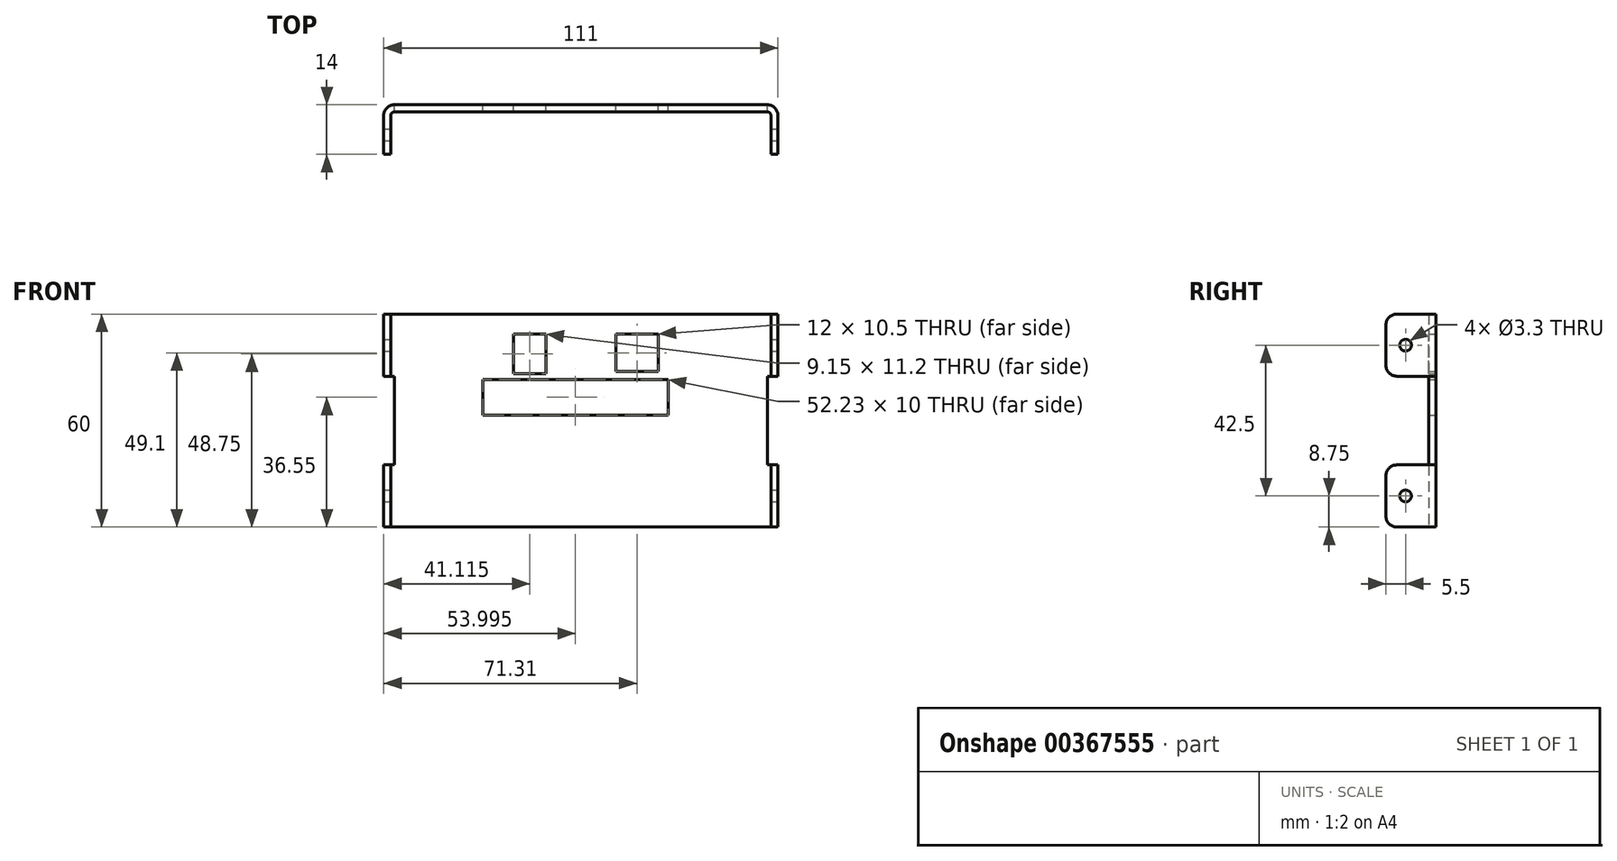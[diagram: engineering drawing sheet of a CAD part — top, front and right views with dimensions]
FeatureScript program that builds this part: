
annotation { "Feature Type Name" : "Feature", "Feature Type Description" : "" }
export const myFeature = defineFeature(function(context is Context, id is Id, definition is map)
    precondition{}
    {
        {
            var Q0;
            Q0=qCreatedBy(makeId("Top.planeOp"),FACE);
            var sketch = newSketch(context, id + "F0", { "sketchPlane" : qUnion([Q0])});
            skLineSegment(sketch, "E0", {"start": v(52.5, 0) * mm, "end": v(-52.5, 0) * mm});
            skLineSegment(sketch, "E1", {"start": v(-53.5, -1) * mm, "end": v(-53.5, -12) * mm});
            skLineSegment(sketch, "E2", {"start": v(53.5, -1) * mm, "end": v(53.5, -12) * mm});
            skPoint(sketch, "E3", {"position": v(0, 0) * mm});
            skPoint(sketch, "E4.visualSharp", {"position": v(-53.5, 0) * mm});
            skArc(sketch, "E4.filletArc", {"start": v(-52.5, 0) * mm, "mid": v(-53.2, -0.3) * mm, "end": v(-53.5, -1) * mm});
            skPoint(sketch, "E5.visualSharp", {"position": v(53.5, 0) * mm});
            skArc(sketch, "E5.filletArc", {"start": v(53.5, -1) * mm, "mid": v(53.2, -0.3) * mm, "end": v(52.5, 0) * mm});
            skLineSegment(sketch, "E6.0", {"start": v(-55.5, -1) * mm, "end": v(-55.5, -12) * mm});
            skLineSegment(sketch, "E6.1", {"start": v(55.5, -1) * mm, "end": v(55.5, -12) * mm});
            skArc(sketch, "E6.2", {"start": v(55.5, -1) * mm, "mid": v(54.62, 1.12) * mm, "end": v(52.5, 2) * mm});
            skLineSegment(sketch, "E6.3", {"start": v(52.5, 2) * mm, "end": v(-52.5, 2) * mm});
            skArc(sketch, "E6.4", {"start": v(-52.5, 2) * mm, "mid": v(-54.62, 1.12) * mm, "end": v(-55.5, -1) * mm});
            skLineSegment(sketch, "E7", {"start": v(-55.5, -12) * mm, "end": v(-53.5, -12) * mm});
            skLineSegment(sketch, "E8", {"start": v(53.5, -12) * mm, "end": v(55.5, -12) * mm});
            skSolve(sketch);
        }
        {
            var Q0;
            Q0=makeQuery(id+"F0.imprint","IMPRINT",FACE,{"disambiguationData":[TD([[makeQuery(id+"F0.imprint","IMPRINT",EDGE,{"derivedFrom":sQuery(id+"F0.wireOp",EDGE,"E0")}),-1.0]])]});
            extrude(context, id + "F1", {"entities" : qUnion([Q0]), "endBound" : BoundingType.SYMMETRIC, "depth" : 60 * mm});
        }
        {
            var Q0;
            Q0=makeQuery(id+"F1.opExtrude","SWEPT_FACE",FACE,{"disambiguationData":[OSD([sQuery(id+"F0.wireOp",EDGE,"E6.3")])]});
            var sketch = newSketch(context, id + "F2", { "sketchPlane" : qUnion([Q0])});
            skLineSegment(sketch, "E9.0", {"start": v(-55.5, 30) * mm, "end": v(-55.5, -30) * mm, "construction": true});
            skLineSegment(sketch, "E10.0", {"start": v(55.5, 30) * mm, "end": v(55.5, -30) * mm, "construction": true});
            skLineSegment(sketch, "E11.bottom", {"start": v(-55.5, 12.5) * mm, "end": v(-52.5, 12.5) * mm});
            skLineSegment(sketch, "E11.top", {"start": v(-55.5, -12.5) * mm, "end": v(-52.5, -12.5) * mm});
            skLineSegment(sketch, "E11.left", {"start": v(-55.5, 12.5) * mm, "end": v(-55.5, -12.5) * mm});
            skLineSegment(sketch, "E11.right", {"start": v(-52.5, 12.5) * mm, "end": v(-52.5, -12.5) * mm});
            skPoint(sketch, "E12", {"position": v(-52.5, 0) * mm});
            skLineSegment(sketch, "E13", {"start": v(0, 0) * mm, "end": v(0, 30) * mm, "construction": true});
            skLineSegment(sketch, "E14.MirrorCS", {"start": v(55.5, 12.5) * mm, "end": v(52.5, 12.5) * mm});
            skLineSegment(sketch, "E15.MirrorCS", {"start": v(55.5, -12.5) * mm, "end": v(52.5, -12.5) * mm});
            skPoint(sketch, "E16.MirrorP", {"position": v(52.5, 0) * mm});
            skLineSegment(sketch, "E17.MirrorCS", {"start": v(55.5, 12.5) * mm, "end": v(55.5, -12.5) * mm});
            skLineSegment(sketch, "E18.MirrorCS", {"start": v(52.5, 12.5) * mm, "end": v(52.5, -12.5) * mm});
            skLineSegment(sketch, "E19", {"start": v(-17.5, 26) * mm, "end": v(17.5, 26) * mm, "construction": true});
            skPoint(sketch, "E20", {"position": v(0, 26) * mm});
            skLineSegment(sketch, "E21.bottom", {"start": v(-21.81, 24.35) * mm, "end": v(-9.8, 24.35) * mm});
            skLineSegment(sketch, "E21.top", {"start": v(-21.81, 13.85) * mm, "end": v(-9.8, 13.85) * mm});
            skLineSegment(sketch, "E21.left", {"start": v(-21.81, 24.35) * mm, "end": v(-21.81, 13.85) * mm});
            skLineSegment(sketch, "E21.right", {"start": v(-9.8, 24.35) * mm, "end": v(-9.8, 13.85) * mm});
            skLineSegment(sketch, "E22.bottom", {"start": v(9.8, 24.35) * mm, "end": v(18.96, 24.35) * mm});
            skLineSegment(sketch, "E22.top", {"start": v(9.81, 13.15) * mm, "end": v(18.96, 13.15) * mm});
            skLineSegment(sketch, "E22.left", {"start": v(9.8, 24.35) * mm, "end": v(9.81, 13.15) * mm});
            skLineSegment(sketch, "E22.right", {"start": v(18.96, 24.35) * mm, "end": v(18.96, 13.15) * mm});
            skLineSegment(sketch, "E23", {"start": v(9.8, 24.35) * mm, "end": v(-9.8, 24.35) * mm, "construction": true});
            skPoint(sketch, "E24", {"position": v(0, 24.35) * mm});
            skLineSegment(sketch, "E25.bottom", {"start": v(-24.61, 11.55) * mm, "end": v(27.62, 11.55) * mm});
            skLineSegment(sketch, "E25.top", {"start": v(-24.61, 1.55) * mm, "end": v(27.62, 1.55) * mm});
            skLineSegment(sketch, "E25.left", {"start": v(-24.61, 11.55) * mm, "end": v(-24.61, 1.55) * mm});
            skLineSegment(sketch, "E25.right", {"start": v(27.62, 11.55) * mm, "end": v(27.62, 1.55) * mm});
            skSolve(sketch);
        }
        {
            var Q0;
            Q0=makeQuery(id+"F2.imprint","IMPRINT",FACE,{"disambiguationData":[TD([[makeQuery(id+"F2.imprint","IMPRINT",EDGE,{"derivedFrom":sQuery(id+"F2.wireOp",EDGE,"E11.bottom")}),-1.0]])]});
            var Q1;
            Q1=makeQuery(id+"F2.imprint","IMPRINT",FACE,{"disambiguationData":[TD([[makeQuery(id+"F2.imprint","IMPRINT",EDGE,{"derivedFrom":sQuery(id+"F2.wireOp",EDGE,"E14.MirrorCS")}),1.0]])]});
            var Q2;
            Q2=makeQuery(id+"F2.imprint","IMPRINT",FACE,{"disambiguationData":[TD([[makeQuery(id+"F2.imprint","IMPRINT",EDGE,{"derivedFrom":sQuery(id+"F2.wireOp",EDGE,"E21.bottom")}),-1.0]])]});
            var Q3;
            Q3=makeQuery(id+"F2.imprint","IMPRINT",FACE,{"disambiguationData":[TD([[makeQuery(id+"F2.imprint","IMPRINT",EDGE,{"derivedFrom":sQuery(id+"F2.wireOp",EDGE,"E22.bottom")}),-1.0]])]});
            var Q4;
            Q4=makeQuery(id+"F2.imprint","IMPRINT",FACE,{"disambiguationData":[TD([[makeQuery(id+"F2.imprint","IMPRINT",EDGE,{"derivedFrom":sQuery(id+"F2.wireOp",EDGE,"E25.bottom")}),-1.0]])]});
            extrude(context, id + "F3", {"entities" : qUnion([Q0, Q1, Q2, Q3, Q4]), "operationType" : NewBodyOperationType.REMOVE, "endBound" : BoundingType.THROUGH_ALL, "oppositeDirection" : true, "depth" : 25 * mm});
        }
        {
            var Q0;
            {var subQ2=sQuery(id+"F0.wireOp",EDGE,"E6.1");Q0=makeQuery(id+"F3.boolean.opBoolean","SPLIT",FACE,{"disambiguationData":[TD([makeQuery(id+"F3.opExtrude","SWEPT_FACE",FACE,{"disambiguationData":[OSD([sQuery(id+"F2.wireOp",EDGE,"E11.bottom")])]})])],"derivedFrom":makeQuery(id+"F1.opExtrude","SWEPT_FACE",FACE,{"disambiguationData":[OSD([subQ2])]})});}
            var sketch = newSketch(context, id + "F4", { "sketchPlane" : qUnion([Q0])});
            skLineSegment(sketch, "E26", {"start": v(-1, 12.5) * mm, "end": v(-12, 30) * mm, "construction": true});
            skLineSegment(sketch, "E27.0.0", {"start": v(-1, -12.5) * mm, "end": v(-12, -12.5) * mm, "construction": true});
            skLineSegment(sketch, "E27.0.1", {"start": v(-12, -12.5) * mm, "end": v(-12, -30) * mm, "construction": true});
            skLineSegment(sketch, "E27.0.2", {"start": v(-12, -30) * mm, "end": v(-1, -30) * mm, "construction": true});
            skLineSegment(sketch, "E27.0.3", {"start": v(-1, -30) * mm, "end": v(-1, -12.5) * mm, "construction": true});
            skLineSegment(sketch, "E28", {"start": v(-1, -30) * mm, "end": v(-12, -12.5) * mm, "construction": true});
            skPoint(sketch, "E29", {"position": v(-6.5, 21.25) * mm});
            skPoint(sketch, "E30", {"position": v(-6.5, -21.25) * mm});
            skSolve(sketch);
        }
        {
            var Q0;
            Q0=sQuery(id+"F4.wireOp",VERTEX,"E29");
            var Q1;
            Q1=sQuery(id+"F4.wireOp",VERTEX,"E30");
            var Q2;
            Q2=makeQuery(id+"F1.opExtrude","SWEPT_BODY",BODY,{"disambiguationData":[OSD([sQuery(id+"F0.wireOp",EDGE,"E0"),sQuery(id+"F0.wireOp",EDGE,"E1"),sQuery(id+"F0.wireOp",EDGE,"E2"),sQuery(id+"F0.wireOp",EDGE,"E4.filletArc"),sQuery(id+"F0.wireOp",EDGE,"E5.filletArc"),sQuery(id+"F0.wireOp",EDGE,"E6.0"),sQuery(id+"F0.wireOp",EDGE,"E6.1"),sQuery(id+"F0.wireOp",EDGE,"E6.2"),sQuery(id+"F0.wireOp",EDGE,"E6.3"),sQuery(id+"F0.wireOp",EDGE,"E6.4"),sQuery(id+"F0.wireOp",EDGE,"E7"),sQuery(id+"F0.wireOp",EDGE,"E8")])]});
            hole(context, id + "F5", {"style" : HoleStyle.SIMPLE, "endStyle" : HoleEndStyle.THROUGH, "standardTappedOrClearance" : lookupTablePath({ "standard" : "ISO", "fit" : "Normal", "size" : "M3", "type" : "Clearance" }), "standardBlindInLast" : lookupTablePath({ "fit" : "Standard", "standard" : "ISO", "size" : "M3", "type" : "Clearance" }), "holeDiameter" : 3.3 * mm, "tappedDepth" : 12 * mm, "tapClearance" : 3, "locations" : qUnion([Q0, Q1]), "scope" : qUnion([Q2])});
        }
        {
            var Q0;
            Q0=makeQuery(id+"F1.opExtrude","CAP_EDGE",EDGE,{"disambiguationData":[OSD([sQuery(id+"F0.wireOp",EDGE,"E7")])],"isStart":false});
            var Q1;
            Q1=makeQuery(id+"F3.boolean.opBoolean","INTERSECT",EDGE,{"derivedFrom":[makeQuery(id+"F1.opExtrude","SWEPT_FACE",FACE,{"disambiguationData":[OSD([sQuery(id+"F0.wireOp",EDGE,"E7")])]}),makeQuery(id+"F3.opExtrude","SWEPT_FACE",FACE,{"disambiguationData":[OSD([sQuery(id+"F2.wireOp",EDGE,"E14.MirrorCS")])]})]});
            var Q2;
            Q2=makeQuery(id+"F3.boolean.opBoolean","INTERSECT",EDGE,{"derivedFrom":[makeQuery(id+"F1.opExtrude","SWEPT_FACE",FACE,{"disambiguationData":[OSD([sQuery(id+"F0.wireOp",EDGE,"E7")])]}),makeQuery(id+"F3.opExtrude","SWEPT_FACE",FACE,{"disambiguationData":[OSD([sQuery(id+"F2.wireOp",EDGE,"E15.MirrorCS")])]})]});
            var Q3;
            Q3=makeQuery(id+"F1.opExtrude","CAP_EDGE",EDGE,{"disambiguationData":[OSD([sQuery(id+"F0.wireOp",EDGE,"E7")])],"isStart":true});
            var Q4;
            Q4=makeQuery(id+"F1.opExtrude","CAP_EDGE",EDGE,{"disambiguationData":[OSD([sQuery(id+"F0.wireOp",EDGE,"E8")])],"isStart":false});
            var Q5;
            Q5=makeQuery(id+"F3.boolean.opBoolean","INTERSECT",EDGE,{"derivedFrom":[makeQuery(id+"F1.opExtrude","SWEPT_FACE",FACE,{"disambiguationData":[OSD([sQuery(id+"F0.wireOp",EDGE,"E8")])]}),makeQuery(id+"F3.opExtrude","SWEPT_FACE",FACE,{"disambiguationData":[OSD([sQuery(id+"F2.wireOp",EDGE,"E11.bottom")])]})]});
            var Q6;
            Q6=makeQuery(id+"F3.boolean.opBoolean","INTERSECT",EDGE,{"derivedFrom":[makeQuery(id+"F1.opExtrude","SWEPT_FACE",FACE,{"disambiguationData":[OSD([sQuery(id+"F0.wireOp",EDGE,"E8")])]}),makeQuery(id+"F3.opExtrude","SWEPT_FACE",FACE,{"disambiguationData":[OSD([sQuery(id+"F2.wireOp",EDGE,"E11.top")])]})]});
            var Q7;
            Q7=makeQuery(id+"F1.opExtrude","CAP_EDGE",EDGE,{"disambiguationData":[OSD([sQuery(id+"F0.wireOp",EDGE,"E8")])],"isStart":true});
            fillet(context, id + "F6", {"entities" : qUnion([Q0, Q1, Q2, Q3, Q4, Q5, Q6, Q7]), "radius" : 3 * mm, "tangentPropagation" : true, "allowEdgeOverflow" : false});
        }
    });
